FREECAD ASSEMBLY — COMPONENT RECIPES ("30_shelf_base_assembly")

This assembly document has 5 components, labeled P0..P4 below (a component is one placed body or linked part). 0 of them carry a construction recipe — the FreeCAD feature program that regenerates the part from scratch, quoted from this document or its linked companion documents; the rest are supplied as boundary geometry only. No exploded tour is included for this assembly.
COMPONENT P0 — geometry summary ("Body"; no construction recipe available for this part):
  bounding box: 1230.0 x 200.0 x 18.0 mm
  tessellated surface: 12 triangles
  volume: 4428000 mm^3 (100% of its bounding box)
  symmetry: 2-fold rotationally symmetric about the x axis; 2-fold rotationally symmetric about the z axis; mirror-symmetric across its x mid-plane, y mid-plane, z mid-plane
COMPONENT P1 — geometry summary ("Body001"; no construction recipe available for this part):
  bounding box: 200.0 x 139.0 x 18.0 mm
  tessellated surface: 12 triangles
  volume: 500400 mm^3 (100% of its bounding box)
  symmetry: 2-fold rotationally symmetric about the x axis; 2-fold rotationally symmetric about the y axis; 2-fold rotationally symmetric about the z axis; mirror-symmetric across its x mid-plane, y mid-plane, z mid-plane
COMPONENT P2 — geometry summary ("Body002"; no construction recipe available for this part):
  bounding box: 200.0 x 139.0 x 18.0 mm
  tessellated surface: 12 triangles
  volume: 500400 mm^3 (100% of its bounding box)
  symmetry: 2-fold rotationally symmetric about the x axis; 2-fold rotationally symmetric about the y axis; 2-fold rotationally symmetric about the z axis; mirror-symmetric across its x mid-plane, y mid-plane, z mid-plane
COMPONENT P3 — geometry summary ("Body003"; no construction recipe available for this part):
  bounding box: 200.0 x 139.0 x 18.0 mm
  tessellated surface: 12 triangles
  volume: 500400 mm^3 (100% of its bounding box)
  symmetry: 2-fold rotationally symmetric about the x axis; 2-fold rotationally symmetric about the y axis; 2-fold rotationally symmetric about the z axis; mirror-symmetric across its x mid-plane, y mid-plane, z mid-plane
COMPONENT P4 — geometry summary ("Body004"; no construction recipe available for this part):
  bounding box: 1230.0 x 200.0 x 18.0 mm
  tessellated surface: 12 triangles
  volume: 4428000 mm^3 (100% of its bounding box)
  symmetry: 2-fold rotationally symmetric about the x axis; 2-fold rotationally symmetric about the z axis; mirror-symmetric across its x mid-plane, y mid-plane, z mid-plane
PROVENANCE & LICENSES
A FreeCAD (.FCStd) document from a public repository crawl; recipes are the document's own serialized feature recipes (and, for linked parts, companion documents' recipes).
License: as declared in the source repository (recorded in the dataset sidecar).
